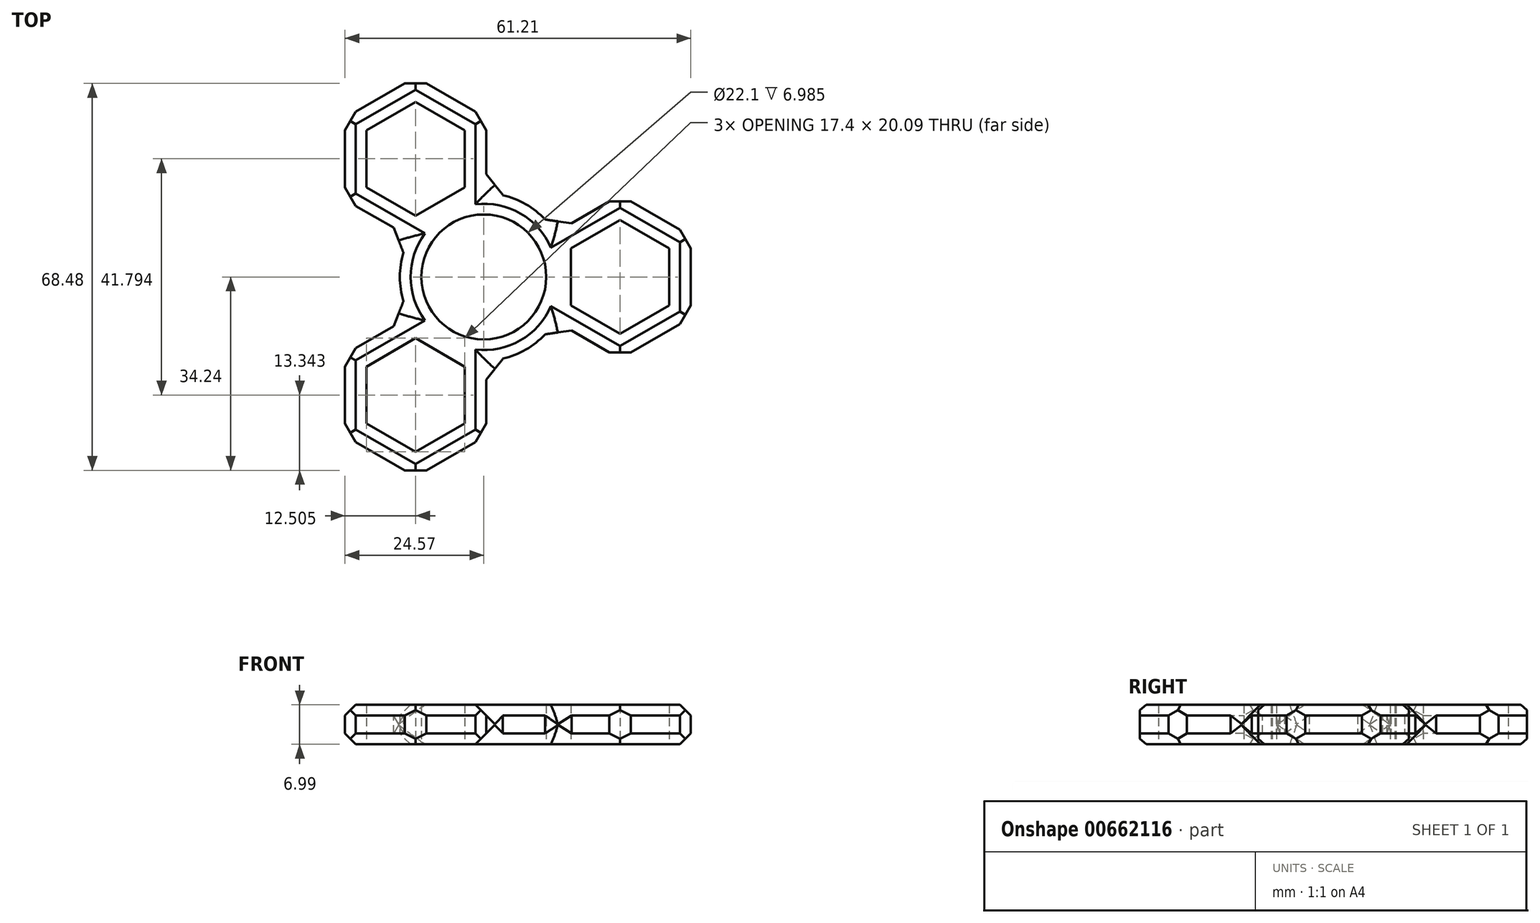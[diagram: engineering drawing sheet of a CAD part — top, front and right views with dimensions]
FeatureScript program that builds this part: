
annotation { "Feature Type Name" : "Feature", "Feature Type Description" : "" }
export const myFeature = defineFeature(function(context is Context, id is Id, definition is map)
    precondition{}
    {
        {
            var Q0;
            Q0=qCreatedBy(makeId("Top.planeOp"),FACE);
            var sketch = newSketch(context, id + "F0", { "sketchPlane" : qUnion([Q0])});
            skCircle(sketch, "E0", {"center": v(0, 0) * mm, "radius": 11.05 * mm});
            skCircle(sketch, "E1.cCircle", {"center": v(24.13, 0) * mm, "radius": 8.7 * mm, "construction": true});
            skLineSegment(sketch, "E1.0", {"start": v(15.43, -5.02) * mm, "end": v(15.43, 5.02) * mm});
            skLineSegment(sketch, "E1.1", {"start": v(15.43, 5.02) * mm, "end": v(24.13, 10.05) * mm});
            skLineSegment(sketch, "E1.2", {"start": v(24.13, 10.05) * mm, "end": v(32.83, 5.02) * mm});
            skLineSegment(sketch, "E1.3", {"start": v(32.83, 5.02) * mm, "end": v(32.83, -5.02) * mm});
            skLineSegment(sketch, "E1.4", {"start": v(32.83, -5.02) * mm, "end": v(24.13, -10.05) * mm});
            skLineSegment(sketch, "E1.5", {"start": v(24.13, -10.05) * mm, "end": v(15.43, -5.02) * mm});
            skPoint(sketch, "E1.0.midPoint", {"position": v(15.43, 0) * mm});
            skLineSegment(sketch, "E2.1.0", {"start": v(-12.06, 30.94) * mm, "end": v(-3.37, 25.92) * mm});
            skLineSegment(sketch, "E2.1.1", {"start": v(-20.76, 15.87) * mm, "end": v(-20.76, 25.92) * mm});
            skLineSegment(sketch, "E2.1.2", {"start": v(-20.76, 25.92) * mm, "end": v(-12.06, 30.94) * mm});
            skPoint(sketch, "E2.1.3", {"position": v(-7.72, 13.36) * mm});
            skLineSegment(sketch, "E2.1.4", {"start": v(-3.37, 15.87) * mm, "end": v(-12.06, 10.85) * mm});
            skLineSegment(sketch, "E2.1.5", {"start": v(-3.37, 25.92) * mm, "end": v(-3.37, 15.87) * mm});
            skCircle(sketch, "E2.1.6", {"center": v(-12.06, 20.9) * mm, "radius": 8.7 * mm, "construction": true});
            skLineSegment(sketch, "E2.1.7", {"start": v(-12.06, 10.85) * mm, "end": v(-20.76, 15.87) * mm});
            skLineSegment(sketch, "E2.2.0", {"start": v(-20.76, -25.92) * mm, "end": v(-20.76, -15.87) * mm});
            skLineSegment(sketch, "E2.2.1", {"start": v(-3.37, -25.92) * mm, "end": v(-12.07, -30.94) * mm});
            skLineSegment(sketch, "E2.2.2", {"start": v(-12.07, -30.94) * mm, "end": v(-20.76, -25.92) * mm});
            skPoint(sketch, "E2.2.3", {"position": v(-7.72, -13.36) * mm});
            skLineSegment(sketch, "E2.2.4", {"start": v(-12.07, -10.85) * mm, "end": v(-3.37, -15.87) * mm});
            skLineSegment(sketch, "E2.2.5", {"start": v(-20.76, -15.87) * mm, "end": v(-12.07, -10.85) * mm});
            skCircle(sketch, "E2.2.6", {"center": v(-12.07, -20.9) * mm, "radius": 8.7 * mm, "construction": true});
            skLineSegment(sketch, "E2.2.7", {"start": v(-3.37, -15.87) * mm, "end": v(-3.37, -25.92) * mm});
            skLineSegment(sketch, "E3.0", {"start": v(-24.57, 28.12) * mm, "end": v(-12.07, 35.34) * mm});
            skLineSegment(sketch, "E3.1", {"start": v(0.44, 28.12) * mm, "end": v(0.44, 14.85) * mm});
            skLineSegment(sketch, "E3.3", {"start": v(-12.07, 35.34) * mm, "end": v(0.44, 28.12) * mm});
            skLineSegment(sketch, "E3.4", {"start": v(-13.08, 7.04) * mm, "end": v(-24.57, 13.67) * mm});
            skLineSegment(sketch, "E3.5", {"start": v(-24.57, 13.67) * mm, "end": v(-24.57, 28.12) * mm});
            skLineSegment(sketch, "E4.0", {"start": v(12.64, 7.81) * mm, "end": v(24.13, 14.44) * mm});
            skLineSegment(sketch, "E4.1", {"start": v(36.64, 7.22) * mm, "end": v(36.64, -7.22) * mm});
            skLineSegment(sketch, "E4.2", {"start": v(36.64, -7.22) * mm, "end": v(24.13, -14.44) * mm});
            skLineSegment(sketch, "E4.3", {"start": v(24.13, 14.44) * mm, "end": v(36.64, 7.22) * mm});
            skLineSegment(sketch, "E4.4", {"start": v(24.13, -14.44) * mm, "end": v(12.64, -7.81) * mm});
            skLineSegment(sketch, "E5.0", {"start": v(0.44, -28.12) * mm, "end": v(-12.07, -35.34) * mm});
            skLineSegment(sketch, "E5.1", {"start": v(-24.57, -28.12) * mm, "end": v(-24.57, -13.67) * mm});
            skLineSegment(sketch, "E5.2", {"start": v(-24.57, -13.67) * mm, "end": v(-13.08, -7.04) * mm});
            skLineSegment(sketch, "E5.3", {"start": v(-12.07, -35.34) * mm, "end": v(-24.57, -28.12) * mm});
            skLineSegment(sketch, "E5.5", {"start": v(0.44, -14.85) * mm, "end": v(0.44, -28.12) * mm});
            skArc(sketch, "E6.0", {"start": v(12.64, 7.81) * mm, "mid": v(7.43, 12.87) * mm, "end": v(0.44, 14.85) * mm});
            skArc(sketch, "E7.trimOffspring", {"start": v(0.44, -14.85) * mm, "mid": v(7.43, -12.87) * mm, "end": v(12.64, -7.81) * mm});
            skArc(sketch, "E8.trimOffspring", {"start": v(-13.08, 7.04) * mm, "mid": v(-14.86, 0) * mm, "end": v(-13.08, -7.04) * mm});
            skSolve(sketch);
        }
        {
            var Q0;
            Q0=makeQuery(id+"F0.imprint","IMPRINT",FACE,{"disambiguationData":[TD([[makeQuery(id+"F0.imprint","IMPRINT",EDGE,{"derivedFrom":sQuery(id+"F0.wireOp",EDGE,"E0")}),-1.0]])]});
            extrude(context, id + "F1", {"entities" : qUnion([Q0]), "depth" : 7 * mm, "offsetDistance" : 25.4 * mm});
        }
        {
            var Q0;
            Q0=makeQuery(id+"F1.opExtrude","CAP_EDGE",EDGE,{"disambiguationData":[OSD([sQuery(id+"F0.wireOp",EDGE,"E8.trimOffspring")])],"isStart":true});
            var Q1;
            Q1=makeQuery(id+"F1.opExtrude","CAP_EDGE",EDGE,{"disambiguationData":[OSD([sQuery(id+"F0.wireOp",EDGE,"E3.4")])],"isStart":true});
            var Q2;
            Q2=makeQuery(id+"F1.opExtrude","CAP_EDGE",EDGE,{"disambiguationData":[OSD([sQuery(id+"F0.wireOp",EDGE,"E3.5")])],"isStart":true});
            var Q3;
            Q3=makeQuery(id+"F1.opExtrude","CAP_EDGE",EDGE,{"disambiguationData":[OSD([sQuery(id+"F0.wireOp",EDGE,"E3.0")])],"isStart":true});
            var Q4;
            Q4=makeQuery(id+"F1.opExtrude","CAP_EDGE",EDGE,{"disambiguationData":[OSD([sQuery(id+"F0.wireOp",EDGE,"E3.3")])],"isStart":true});
            var Q5;
            Q5=makeQuery(id+"F1.opExtrude","CAP_EDGE",EDGE,{"disambiguationData":[OSD([sQuery(id+"F0.wireOp",EDGE,"E3.1")])],"isStart":true});
            var Q6;
            Q6=makeQuery(id+"F1.opExtrude","CAP_EDGE",EDGE,{"disambiguationData":[OSD([sQuery(id+"F0.wireOp",EDGE,"E6.0")])],"isStart":true});
            var Q7;
            Q7=makeQuery(id+"F1.opExtrude","CAP_EDGE",EDGE,{"disambiguationData":[OSD([sQuery(id+"F0.wireOp",EDGE,"E4.0")])],"isStart":true});
            var Q8;
            Q8=makeQuery(id+"F1.opExtrude","CAP_EDGE",EDGE,{"disambiguationData":[OSD([sQuery(id+"F0.wireOp",EDGE,"E4.3")])],"isStart":true});
            var Q9;
            Q9=makeQuery(id+"F1.opExtrude","CAP_EDGE",EDGE,{"disambiguationData":[OSD([sQuery(id+"F0.wireOp",EDGE,"E4.1")])],"isStart":true});
            var Q10;
            Q10=makeQuery(id+"F1.opExtrude","CAP_EDGE",EDGE,{"disambiguationData":[OSD([sQuery(id+"F0.wireOp",EDGE,"E4.2")])],"isStart":true});
            var Q11;
            Q11=makeQuery(id+"F1.opExtrude","CAP_EDGE",EDGE,{"disambiguationData":[OSD([sQuery(id+"F0.wireOp",EDGE,"E4.4")])],"isStart":true});
            var Q12;
            Q12=makeQuery(id+"F1.opExtrude","CAP_EDGE",EDGE,{"disambiguationData":[OSD([sQuery(id+"F0.wireOp",EDGE,"E7.trimOffspring")])],"isStart":true});
            var Q13;
            Q13=makeQuery(id+"F1.opExtrude","CAP_EDGE",EDGE,{"disambiguationData":[OSD([sQuery(id+"F0.wireOp",EDGE,"E5.5")])],"isStart":true});
            var Q14;
            Q14=makeQuery(id+"F1.opExtrude","CAP_EDGE",EDGE,{"disambiguationData":[OSD([sQuery(id+"F0.wireOp",EDGE,"E5.0")])],"isStart":true});
            var Q15;
            Q15=makeQuery(id+"F1.opExtrude","CAP_EDGE",EDGE,{"disambiguationData":[OSD([sQuery(id+"F0.wireOp",EDGE,"E5.3")])],"isStart":true});
            var Q16;
            Q16=makeQuery(id+"F1.opExtrude","CAP_EDGE",EDGE,{"disambiguationData":[OSD([sQuery(id+"F0.wireOp",EDGE,"E5.1")])],"isStart":true});
            var Q17;
            Q17=makeQuery(id+"F1.opExtrude","CAP_EDGE",EDGE,{"disambiguationData":[OSD([sQuery(id+"F0.wireOp",EDGE,"E5.2")])],"isStart":true});
            var Q18;
            Q18=makeQuery(id+"F1.opExtrude","CAP_EDGE",EDGE,{"disambiguationData":[OSD([sQuery(id+"F0.wireOp",EDGE,"E8.trimOffspring")])],"isStart":false});
            var Q19;
            Q19=makeQuery(id+"F1.opExtrude","CAP_EDGE",EDGE,{"disambiguationData":[OSD([sQuery(id+"F0.wireOp",EDGE,"E3.4")])],"isStart":false});
            var Q20;
            Q20=makeQuery(id+"F1.opExtrude","CAP_EDGE",EDGE,{"disambiguationData":[OSD([sQuery(id+"F0.wireOp",EDGE,"E3.5")])],"isStart":false});
            var Q21;
            Q21=makeQuery(id+"F1.opExtrude","CAP_EDGE",EDGE,{"disambiguationData":[OSD([sQuery(id+"F0.wireOp",EDGE,"E3.0")])],"isStart":false});
            var Q22;
            Q22=makeQuery(id+"F1.opExtrude","CAP_EDGE",EDGE,{"disambiguationData":[OSD([sQuery(id+"F0.wireOp",EDGE,"E3.3")])],"isStart":false});
            var Q23;
            Q23=makeQuery(id+"F1.opExtrude","CAP_EDGE",EDGE,{"disambiguationData":[OSD([sQuery(id+"F0.wireOp",EDGE,"E3.1")])],"isStart":false});
            var Q24;
            Q24=makeQuery(id+"F1.opExtrude","CAP_EDGE",EDGE,{"disambiguationData":[OSD([sQuery(id+"F0.wireOp",EDGE,"E6.0")])],"isStart":false});
            var Q25;
            Q25=makeQuery(id+"F1.opExtrude","CAP_EDGE",EDGE,{"disambiguationData":[OSD([sQuery(id+"F0.wireOp",EDGE,"E4.0")])],"isStart":false});
            var Q26;
            Q26=makeQuery(id+"F1.opExtrude","CAP_EDGE",EDGE,{"disambiguationData":[OSD([sQuery(id+"F0.wireOp",EDGE,"E4.3")])],"isStart":false});
            var Q27;
            Q27=makeQuery(id+"F1.opExtrude","CAP_EDGE",EDGE,{"disambiguationData":[OSD([sQuery(id+"F0.wireOp",EDGE,"E4.1")])],"isStart":false});
            var Q28;
            Q28=makeQuery(id+"F1.opExtrude","CAP_EDGE",EDGE,{"disambiguationData":[OSD([sQuery(id+"F0.wireOp",EDGE,"E4.2")])],"isStart":false});
            var Q29;
            Q29=makeQuery(id+"F1.opExtrude","CAP_EDGE",EDGE,{"disambiguationData":[OSD([sQuery(id+"F0.wireOp",EDGE,"E4.4")])],"isStart":false});
            var Q30;
            Q30=makeQuery(id+"F1.opExtrude","CAP_EDGE",EDGE,{"disambiguationData":[OSD([sQuery(id+"F0.wireOp",EDGE,"E7.trimOffspring")])],"isStart":false});
            var Q31;
            Q31=makeQuery(id+"F1.opExtrude","CAP_EDGE",EDGE,{"disambiguationData":[OSD([sQuery(id+"F0.wireOp",EDGE,"E5.5")])],"isStart":false});
            var Q32;
            Q32=makeQuery(id+"F1.opExtrude","CAP_EDGE",EDGE,{"disambiguationData":[OSD([sQuery(id+"F0.wireOp",EDGE,"E5.0")])],"isStart":false});
            var Q33;
            Q33=makeQuery(id+"F1.opExtrude","CAP_EDGE",EDGE,{"disambiguationData":[OSD([sQuery(id+"F0.wireOp",EDGE,"E5.3")])],"isStart":false});
            var Q34;
            Q34=makeQuery(id+"F1.opExtrude","CAP_EDGE",EDGE,{"disambiguationData":[OSD([sQuery(id+"F0.wireOp",EDGE,"E5.2")])],"isStart":false});
            var Q35;
            Q35=makeQuery(id+"F1.opExtrude","CAP_EDGE",EDGE,{"disambiguationData":[OSD([sQuery(id+"F0.wireOp",EDGE,"E5.1")])],"isStart":false});
            chamfer(context, id + "F2", {"entities" : qUnion([Q0, Q1, Q2, Q3, Q4, Q5, Q6, Q7, Q8, Q9, Q10, Q11, Q12, Q13, Q14, Q15, Q16, Q17, Q18, Q19, Q20, Q21, Q22, Q23, Q24, Q25, Q26, Q27, Q28, Q29, Q30, Q31, Q32, Q33, Q34, Q35]), "width" : 1.9 * mm, "tangentPropagation" : true});
        }
        {
            var Q0;
            Q0=makeQuery(id+"F1.opExtrude","SWEPT_EDGE",EDGE,{"disambiguationData":[OSD([sQuery(id+"F0.wireOp",EDGE,"E5.5"),sQuery(id+"F0.wireOp",EDGE,"E7.trimOffspring")])]});
            var Q1;
            Q1=makeQuery(id+"F1.opExtrude","SWEPT_EDGE",EDGE,{"disambiguationData":[OSD([sQuery(id+"F0.wireOp",EDGE,"E4.4"),sQuery(id+"F0.wireOp",EDGE,"E7.trimOffspring")])]});
            var Q2;
            Q2=makeQuery(id+"F1.opExtrude","SWEPT_EDGE",EDGE,{"disambiguationData":[OSD([sQuery(id+"F0.wireOp",EDGE,"E4.2"),sQuery(id+"F0.wireOp",EDGE,"E4.4")])]});
            var Q3;
            Q3=makeQuery(id+"F1.opExtrude","SWEPT_EDGE",EDGE,{"disambiguationData":[OSD([sQuery(id+"F0.wireOp",EDGE,"E4.1"),sQuery(id+"F0.wireOp",EDGE,"E4.2")])]});
            var Q4;
            Q4=makeQuery(id+"F1.opExtrude","SWEPT_EDGE",EDGE,{"disambiguationData":[OSD([sQuery(id+"F0.wireOp",EDGE,"E4.1"),sQuery(id+"F0.wireOp",EDGE,"E4.3")])]});
            var Q5;
            Q5=makeQuery(id+"F1.opExtrude","SWEPT_EDGE",EDGE,{"disambiguationData":[OSD([sQuery(id+"F0.wireOp",EDGE,"E4.0"),sQuery(id+"F0.wireOp",EDGE,"E4.3")])]});
            var Q6;
            Q6=makeQuery(id+"F1.opExtrude","SWEPT_EDGE",EDGE,{"disambiguationData":[OSD([sQuery(id+"F0.wireOp",EDGE,"E4.0"),sQuery(id+"F0.wireOp",EDGE,"E6.0")])]});
            var Q7;
            Q7=makeQuery(id+"F1.opExtrude","SWEPT_EDGE",EDGE,{"disambiguationData":[OSD([sQuery(id+"F0.wireOp",EDGE,"E3.1"),sQuery(id+"F0.wireOp",EDGE,"E6.0")])]});
            var Q8;
            Q8=makeQuery(id+"F1.opExtrude","SWEPT_EDGE",EDGE,{"disambiguationData":[OSD([sQuery(id+"F0.wireOp",EDGE,"E3.1"),sQuery(id+"F0.wireOp",EDGE,"E3.3")])]});
            var Q9;
            Q9=makeQuery(id+"F1.opExtrude","SWEPT_EDGE",EDGE,{"disambiguationData":[OSD([sQuery(id+"F0.wireOp",EDGE,"E3.0"),sQuery(id+"F0.wireOp",EDGE,"E3.3")])]});
            var Q10;
            Q10=makeQuery(id+"F1.opExtrude","SWEPT_EDGE",EDGE,{"disambiguationData":[OSD([sQuery(id+"F0.wireOp",EDGE,"E3.0"),sQuery(id+"F0.wireOp",EDGE,"E3.5")])]});
            var Q11;
            Q11=makeQuery(id+"F1.opExtrude","SWEPT_EDGE",EDGE,{"disambiguationData":[OSD([sQuery(id+"F0.wireOp",EDGE,"E3.4"),sQuery(id+"F0.wireOp",EDGE,"E3.5")])]});
            var Q12;
            Q12=makeQuery(id+"F1.opExtrude","SWEPT_EDGE",EDGE,{"disambiguationData":[OSD([sQuery(id+"F0.wireOp",EDGE,"E3.4"),sQuery(id+"F0.wireOp",EDGE,"E8.trimOffspring")])]});
            var Q13;
            Q13=makeQuery(id+"F1.opExtrude","SWEPT_EDGE",EDGE,{"disambiguationData":[OSD([sQuery(id+"F0.wireOp",EDGE,"E5.1"),sQuery(id+"F0.wireOp",EDGE,"E5.2")])]});
            var Q14;
            Q14=makeQuery(id+"F1.opExtrude","SWEPT_EDGE",EDGE,{"disambiguationData":[OSD([sQuery(id+"F0.wireOp",EDGE,"E5.2"),sQuery(id+"F0.wireOp",EDGE,"E8.trimOffspring")])]});
            var Q15;
            Q15=makeQuery(id+"F1.opExtrude","SWEPT_EDGE",EDGE,{"disambiguationData":[OSD([sQuery(id+"F0.wireOp",EDGE,"E5.1"),sQuery(id+"F0.wireOp",EDGE,"E5.3")])]});
            var Q16;
            Q16=makeQuery(id+"F1.opExtrude","SWEPT_EDGE",EDGE,{"disambiguationData":[OSD([sQuery(id+"F0.wireOp",EDGE,"E5.0"),sQuery(id+"F0.wireOp",EDGE,"E5.3")])]});
            var Q17;
            Q17=makeQuery(id+"F1.opExtrude","SWEPT_EDGE",EDGE,{"disambiguationData":[OSD([sQuery(id+"F0.wireOp",EDGE,"E5.0"),sQuery(id+"F0.wireOp",EDGE,"E5.5")])]});
            chamfer(context, id + "F3", {"entities" : qUnion([Q0, Q1, Q2, Q3, Q4, Q5, Q6, Q7, Q8, Q9, Q10, Q11, Q12, Q13, Q14, Q15, Q16, Q17]), "width" : 3.8 * mm, "tangentPropagation" : true});
        }
    });
